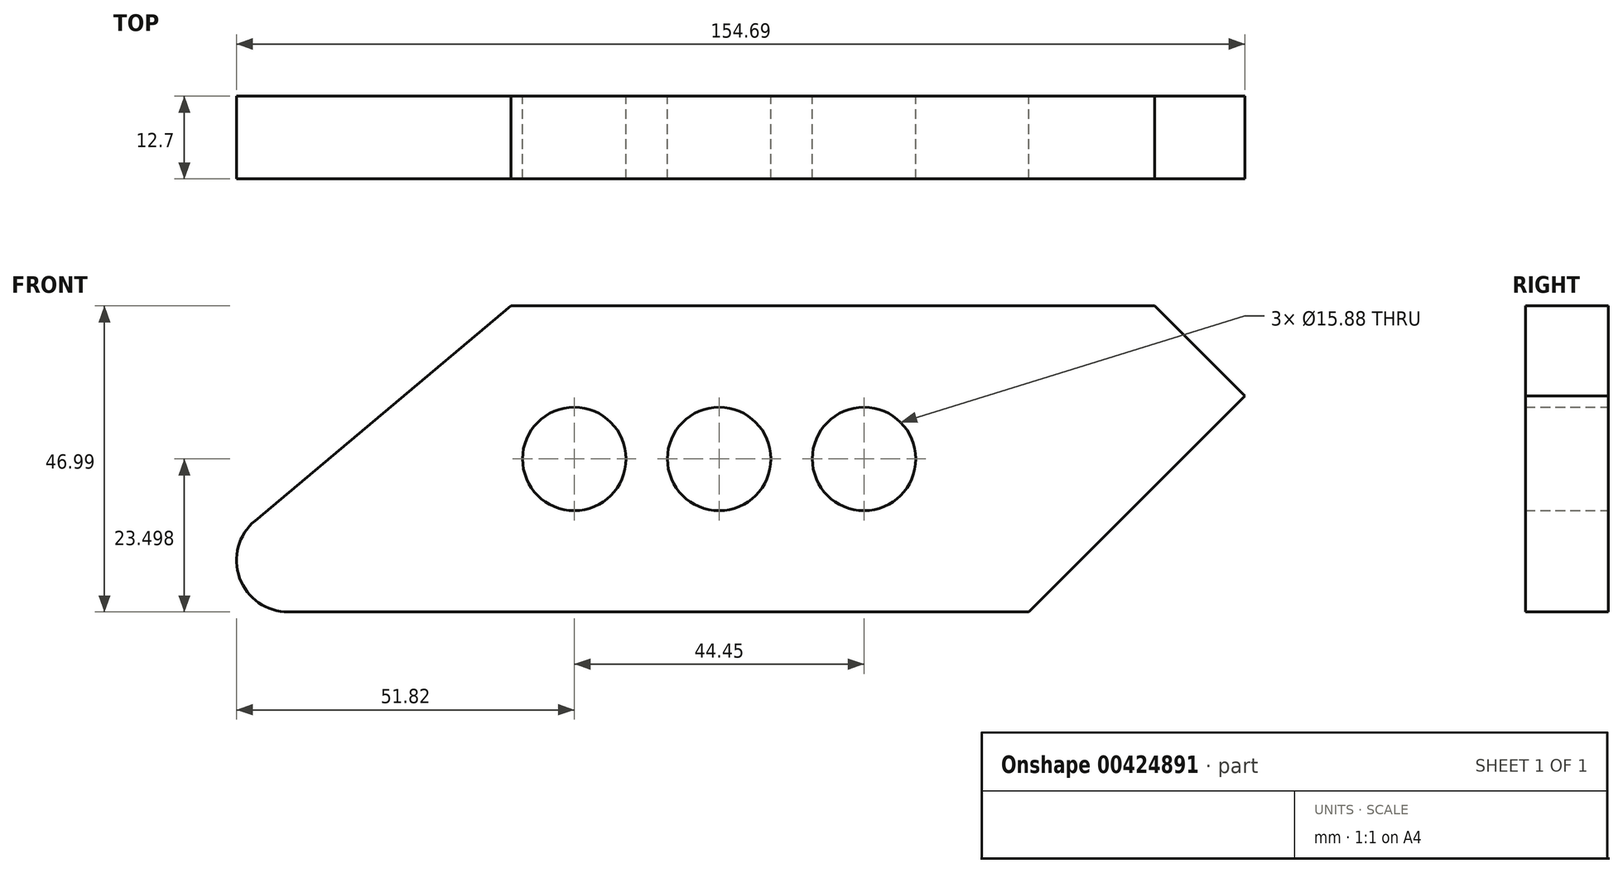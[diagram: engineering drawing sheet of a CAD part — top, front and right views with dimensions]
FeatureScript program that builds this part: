
annotation { "Feature Type Name" : "Feature", "Feature Type Description" : "" }
export const myFeature = defineFeature(function(context is Context, id is Id, definition is map)
    precondition{}
    {
        {
            var Q0;
            Q0=qCreatedBy(makeId("Front.planeOp"),FACE);
            var sketch = newSketch(context, id + "F0", { "sketchPlane" : qUnion([Q0])});
            skLineSegment(sketch, "E0", {"start": v(0, 0) * mm, "end": v(-13.84, 13.84) * mm});
            skLineSegment(sketch, "E1", {"start": v(-13.84, 13.84) * mm, "end": v(-112.56, 13.84) * mm});
            skLineSegment(sketch, "E2", {"start": v(-112.56, 13.84) * mm, "end": v(-151.85, -19.13) * mm});
            skLineSegment(sketch, "E3", {"start": v(-146.75, -33.15) * mm, "end": v(-33.15, -33.15) * mm});
            skLineSegment(sketch, "E4", {"start": v(-33.15, -33.15) * mm, "end": v(0, 0) * mm});
            skPoint(sketch, "E5.visualSharp", {"position": v(-168.56, -33.15) * mm});
            skArc(sketch, "E5.filletArc", {"start": v(-151.85, -19.13) * mm, "mid": v(-154.2, -27.92) * mm, "end": v(-146.75, -33.15) * mm});
            skLineSegment(sketch, "E6", {"start": v(-154.69, 13.55) * mm, "end": v(-154.69, -34.17) * mm, "construction": true});
            skLineSegment(sketch, "E7", {"start": v(-128.29, -9.65) * mm, "end": v(-24.24, -9.65) * mm, "construction": true});
            skCircle(sketch, "E8", {"center": v(-58.42, -9.65) * mm, "radius": 7.94 * mm});
            skCircle(sketch, "E9", {"center": v(-80.64, -9.65) * mm, "radius": 7.94 * mm});
            skCircle(sketch, "E10", {"center": v(-102.87, -9.65) * mm, "radius": 7.94 * mm});
            skSolve(sketch);
        }
        {
            var Q0;
            Q0 = qSketchRegion(id + "F0", true);
            extrude(context, id + "F1", {"entities" : qUnion([Q0]), "depth" : 12.7 * mm});
        }
    });
